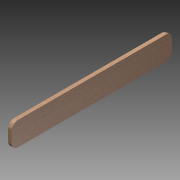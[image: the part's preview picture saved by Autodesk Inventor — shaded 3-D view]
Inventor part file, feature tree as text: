
AUTODESK INVENTOR PART (.ipt)
format: ipt  version: 2014 SP1 (Build 180222100, 222)  size: 100,352 bytes
history: native  units: in
note: dims shown in document units (in); Inventor stores cm internally (conversion verified against a paired STEP export)
features: extrude x1, fillet x1, sketch x1
ambient origin geometry x8: Origin, YZ Plane, XZ Plane, XY Plane, X Axis, Y Axis, Z Axis, Center Point
bodies: Solid1 (feature_tree)
feature tree (3):
  extrude  "Extrusion1"  Depth=0.75in
  fillet  "Fillet1"  Radius=33.625in
  sketch  "Sketch1"  dims[d0=5.0in d1=0.75in d2=33.625in d3=0.0in d4=1.3125in]
